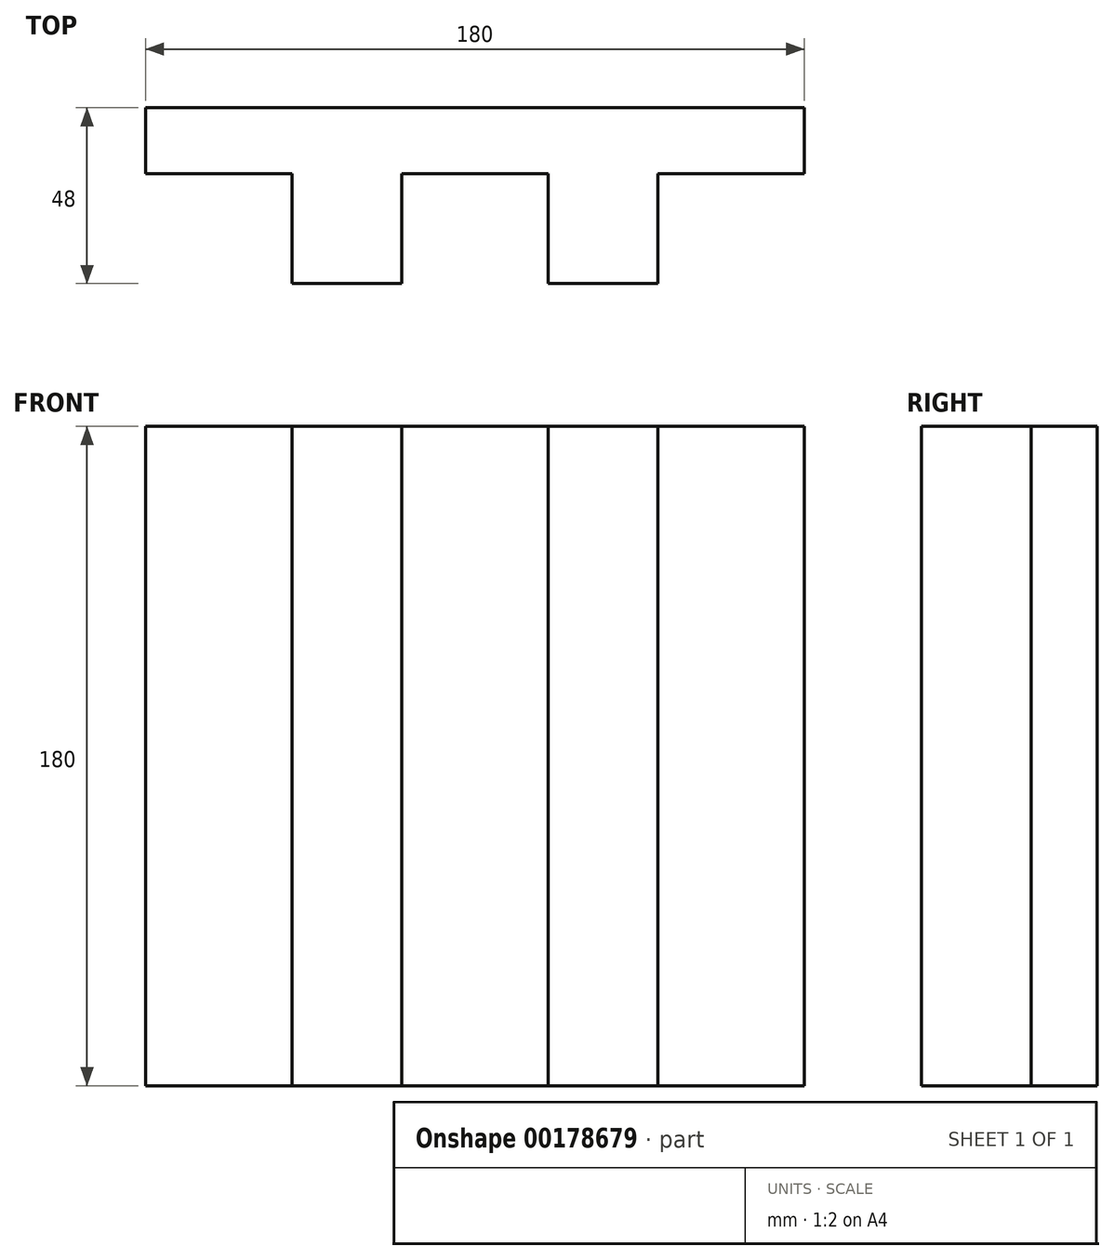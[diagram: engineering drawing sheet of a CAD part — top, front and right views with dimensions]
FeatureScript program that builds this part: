
annotation { "Feature Type Name" : "Feature", "Feature Type Description" : "" }
export const myFeature = defineFeature(function(context is Context, id is Id, definition is map)
    precondition{}
    {
        {
            var Q0;
            Q0=qCreatedBy(makeId("Top.planeOp"),FACE);
            var sketch = newSketch(context, id + "F0", { "sketchPlane" : qUnion([Q0])});
            skLineSegment(sketch, "E0", {"start": v(0, 0) * mm, "end": v(508, 0) * mm});
            skLineSegment(sketch, "E1", {"start": v(508, 0) * mm, "end": v(508, 762) * mm});
            skLineSegment(sketch, "E2", {"start": v(508, 762) * mm, "end": v(1270, 762) * mm});
            skLineSegment(sketch, "E3", {"start": v(1270, 762) * mm, "end": v(1270, 0) * mm});
            skLineSegment(sketch, "E4", {"start": v(1270, 0) * mm, "end": v(2286, 0) * mm});
            skLineSegment(sketch, "E5", {"start": v(2286, 0) * mm, "end": v(2286, -457.2) * mm});
            skLineSegment(sketch, "E6", {"start": v(2286, -457.2) * mm, "end": v(0, -457.2) * mm});
            skLineSegment(sketch, "E7.MirrorCS", {"start": v(-2286, -457.2) * mm, "end": v(0, -457.2) * mm});
            skLineSegment(sketch, "E8.MirrorCS", {"start": v(0, 0) * mm, "end": v(-508, 0) * mm});
            skLineSegment(sketch, "E9.MirrorCS", {"start": v(-1270, 0) * mm, "end": v(-2286, 0) * mm});
            skLineSegment(sketch, "E10.MirrorCS", {"start": v(-508, 0) * mm, "end": v(-508, 762) * mm});
            skLineSegment(sketch, "E11.MirrorCS", {"start": v(-1270, 762) * mm, "end": v(-1270, 0) * mm});
            skLineSegment(sketch, "E12.MirrorCS", {"start": v(-508, 762) * mm, "end": v(-1270, 762) * mm});
            skLineSegment(sketch, "E13", {"start": v(-2286, 0) * mm, "end": v(-2286, -457.2) * mm});
            skSolve(sketch);
        }
        {
            var Q0;
            Q0 = qSketchRegion(id + "F0", true);
            extrude(context, id + "F1", {"entities" : qUnion([Q0]), "depth" : 4572 * mm});
        }
        {
            var Q0;
            Q0=makeQuery(id+"F1.opExtrude","SWEPT_BODY",BODY,{"disambiguationData":[OSD([sQuery(id+"F0.wireOp",EDGE,"E0"),sQuery(id+"F0.wireOp",EDGE,"E1"),sQuery(id+"F0.wireOp",EDGE,"E2"),sQuery(id+"F0.wireOp",EDGE,"E3"),sQuery(id+"F0.wireOp",EDGE,"E4"),sQuery(id+"F0.wireOp",EDGE,"E5"),sQuery(id+"F0.wireOp",EDGE,"E6"),sQuery(id+"F0.wireOp",EDGE,"E7.MirrorCS"),sQuery(id+"F0.wireOp",EDGE,"E8.MirrorCS"),sQuery(id+"F0.wireOp",EDGE,"E9.MirrorCS"),sQuery(id+"F0.wireOp",EDGE,"E10.MirrorCS"),sQuery(id+"F0.wireOp",EDGE,"E11.MirrorCS"),sQuery(id+"F0.wireOp",EDGE,"E12.MirrorCS"),sQuery(id+"F0.wireOp",EDGE,"E13")])]});
            var Q1;
            Q1=qCreatedBy(makeId("Origin.pointOp"),VERTEX);
            transform(context, id + "F2", {"entities" : qUnion([Q0]), "transformType" : TransformType.SCALE_UNIFORMLY, "scale" : 1 / 25.4, "scalePoint" : qUnion([Q1]), "makeCopy" : false});
        }
        {
            var Q0;
            Q0=makeQuery(id+"F1.opExtrude","SWEPT_BODY",BODY,{"disambiguationData":[OSD([sQuery(id+"F0.wireOp",EDGE,"E0"),sQuery(id+"F0.wireOp",EDGE,"E1"),sQuery(id+"F0.wireOp",EDGE,"E2"),sQuery(id+"F0.wireOp",EDGE,"E3"),sQuery(id+"F0.wireOp",EDGE,"E4"),sQuery(id+"F0.wireOp",EDGE,"E5"),sQuery(id+"F0.wireOp",EDGE,"E6"),sQuery(id+"F0.wireOp",EDGE,"E7.MirrorCS"),sQuery(id+"F0.wireOp",EDGE,"E8.MirrorCS"),sQuery(id+"F0.wireOp",EDGE,"E9.MirrorCS"),sQuery(id+"F0.wireOp",EDGE,"E10.MirrorCS"),sQuery(id+"F0.wireOp",EDGE,"E11.MirrorCS"),sQuery(id+"F0.wireOp",EDGE,"E12.MirrorCS"),sQuery(id+"F0.wireOp",EDGE,"E13")])]});
            var Q1;
            Q1=makeQuery(id+"F1.opExtrude","CAP_EDGE",EDGE,{"disambiguationData":[OSD([sQuery(id+"F0.wireOp",EDGE,"E0"),sQuery(id+"F0.wireOp",EDGE,"E8.MirrorCS")])],"isStart":true});
            transform(context, id + "F3", {"entities" : qUnion([Q0]), "transformType" : TransformType.ROTATION, "transformAxis" : qUnion([Q1]), "angle" : 180 * degree, "makeCopy" : false});
        }
    });
